# Revit family: PipeAccessories_AutomaticAirVent_DRBrass_Dura
name_source: partatom
category: Pipe Accessories
units: mm (PartAtom-declared; Revit-internal decimal feet)

## family parameters
Always vertical = Yes
Cut with Voids When Loaded = Yes
OmniClass Number = 23.65.55.14.17
OmniClass Title = Adjusting/Controlling Valves for Liquid Services
Part Type = Valve - Normal
Round Connector Dimension = Use Radius
Shared = No
Work Plane-Based = No

## types (1)
- Automatic AirVent_DR-Brass_Dura
    AirVentHeight = 93 mm
    Assembly Code = D2090800
    BodyMaterial = <By Category>
    BodyRadius = 19.5 mm
    BonnetNo = 20
    Description = Dura Eagle Automatic Airvent is used to remove residual air from the water in a closed heating or cooling system. This helps to reduce noise and improve efficiency of equipment.
    FinalHHWFlow = 0.0 L/s
    H1 = 68.32 mm
    H2 = 24.68 mm
    Height = 60 mm  [stored 0.19685 ft]
    Manufacturer = Reece
    Model = Automatic AirVent_DR-Brass_Dura
    Model Specification = BMA
    Model Version = 2013-03
    NATSPECWorkSection = TBC
    OmniclassProducts = TBC
    ProductCode = 9502880
    Size = 10 mm  [stored 0.0328084 ft]
    SizeRadius = 5 mm  [stored 0.0164042 ft]
    Type Comments = Dura's range of valves ensure you have the right valve for the right application.
Products range from ball valves and gate valves all the way to butterfly and mechanical valves to ensure you have the solution to meet your specification requirements.
    URL = www.reece.com.au
    Uniformat IIElements = TBC

note: [stored X ft] marks values corroborated as IEEE doubles in the binary element streams (Revit-internal decimal feet)

## geometry (parser evidence)
native form markers: Sweep x8
no freeform markers — native parametric forms only
